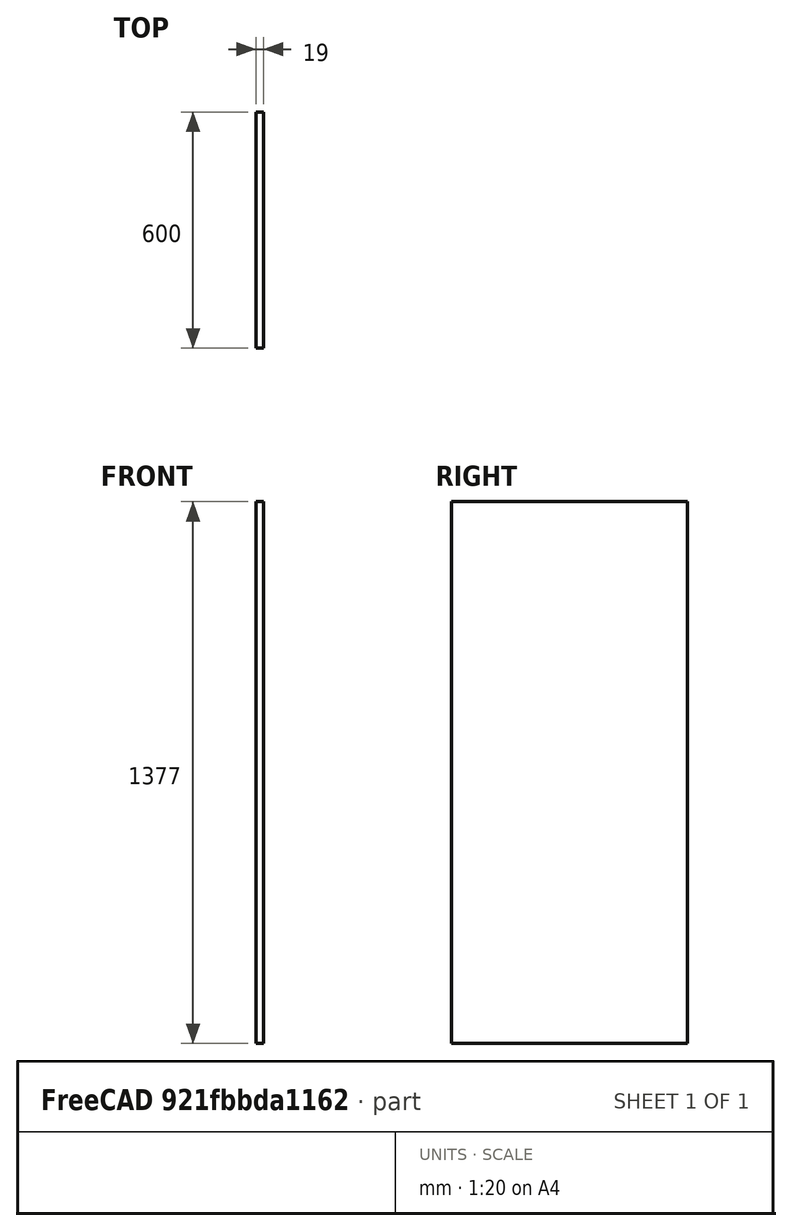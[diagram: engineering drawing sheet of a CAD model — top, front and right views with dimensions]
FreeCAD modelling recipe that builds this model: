
FCSTD DOCUMENT  (FreeCAD 1.0RUnknown)
Label: wardrobe_left_corpus01_jan
License: All rights reserved
LicenseURL: https://en.wikipedia.org/wiki/All_rights_reserved
objects: PartDesign::CoordinateSystem×3, Sketcher::SketchObject×1, PartDesign::Pad×1, PartDesign::Body×1
note: 9 computed .brp shape members not serialized (recipe doc carries the construction recipe); baked Part::Feature solids carry a one-line shape summary decoded from their .brp
EXTERNAL_REF file=../../mastersketch.FCStd obj=Spreadsheet

FEATURE [Sketcher::SketchObject] Sketch001
  ArcFitTolerance = 1e-06
  AttachmentSupport = -> [YZ_Plane001]
  FullyConstrained = true
  MakeInternals = false
  MapMode = 5
  Placement = pos=(0,0,0) rot=(0.57735,0.57735,0.57735;2.0944rad)
  expr: Constraints[10] = mastersketch#Spreadsheet.corpus_depth
  expr: Constraints[11] = mastersketch#Spreadsheet.corpus01_height - 2 * mastersketch#Spreadsheet.corpus_outer_thickness
  sketch-geometry (5):
    g0: LineSegment StartX=-300 StartY=-688.5 StartZ=0 EndX=300 EndY=-688.5 EndZ=0
    g1: LineSegment StartX=300 StartY=-688.5 StartZ=0 EndX=300 EndY=688.5 EndZ=0
    g2: LineSegment StartX=300 StartY=688.5 StartZ=0 EndX=-300 EndY=688.5 EndZ=0
    g3: LineSegment StartX=-300 StartY=688.5 StartZ=0 EndX=-300 EndY=-688.5 EndZ=0
    g4: GeomPoint [constr] X=0 Y=0 Z=0
  constraints (12):
    c: Coincident(g0,g1)
    c: Coincident(g1,g2)
    c: Coincident(g2,g3)
    c: Coincident(g3,g0)
    c: Horizontal(g0)
    c: Horizontal(g2)
    c: Vertical(g1)
    c: Vertical(g3)
    c: Symmetric(g2,g0,g4)
    c: Coincident(g4,g-1)
    c: DistanceX(g0,g0) = 600
    c: DistanceY(g3,g3) = 1377
FEATURE [PartDesign::Pad] Pad001
  Direction = (1,0,0)
  Length = 19
  Length2 = 10
  Placement = pos=(0,0,0) rot=(1,1,1;2.0944rad)
  Profile = -> Sketch001
  ReferenceAxis = -> Sketch001 [N_Axis]
  Refine = true
  Suppressed = false
  Type = 0
  expr: Length = mastersketch#Spreadsheet.corpus_outer_thickness
FEATURE [PartDesign::CoordinateSystem] LCS_bottom
  AttacherType = Attacher::AttachEngine3D
  AttachmentSupport = -> [Pad001]
  MapMode = 45
  Placement = pos=(0,-1.42e-14,-688.5) rot=(0,0.707107,0.707107;3.14159rad)
FEATURE [PartDesign::CoordinateSystem] LCS_top
  AttacherType = Attacher::AttachEngine3D
  AttachmentSupport = -> [Pad001]
  MapMode = 45
  Placement = pos=(0,1.42e-14,688.5) rot=(0,0.707107,0.707107;3.14159rad)
FEATURE [PartDesign::CoordinateSystem] LCS_inner
  AttacherType = Attacher::AttachEngine3D
  AttachmentSupport = -> [Pad001]
  MapMode = 45
  Placement = pos=(19,-1.82e-14,-688.5) rot=(0,0.707107,0.707107;3.14159rad)
FEATURE [PartDesign::Body] Body001  label="wardrobe_left_corpus01_jan"
  AllowCompound = false
  Group = -> [Sketch001,Pad001,LCS_bottom,LCS_top,LCS_inner]
  Origin = -> Origin001
  Tip = -> Pad001
